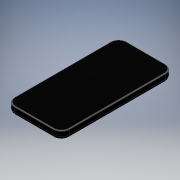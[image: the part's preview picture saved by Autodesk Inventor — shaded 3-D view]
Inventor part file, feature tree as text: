
AUTODESK INVENTOR PART (.ipt)
format: ipt  version: 2016 (Build 200138000, 138)  size: 154,112 bytes
history: native  units: mm
features: fillet x3, extrude x1, sketch x1
ambient origin geometry x8: Origin, YZ Plane, XZ Plane, XY Plane, X Axis, Y Axis, Z Axis, Center Point
bodies: Solid1 (feature_tree)
feature tree (5):
  extrude  "Extrusion1"  Depth=134.62mm
  fillet  "Fillet1"  Radius=10.16mm
  fillet  "Fillet2"  Radius=10.0mm
  fillet  "Fillet3"  Radius=4.0mm
  sketch  "Sketch1"  dims[d0=66.04mm d1=134.62mm d2=10.16mm d3=0.0mm d4=10.0mm d5=4.0mm d6=1.0mm]
